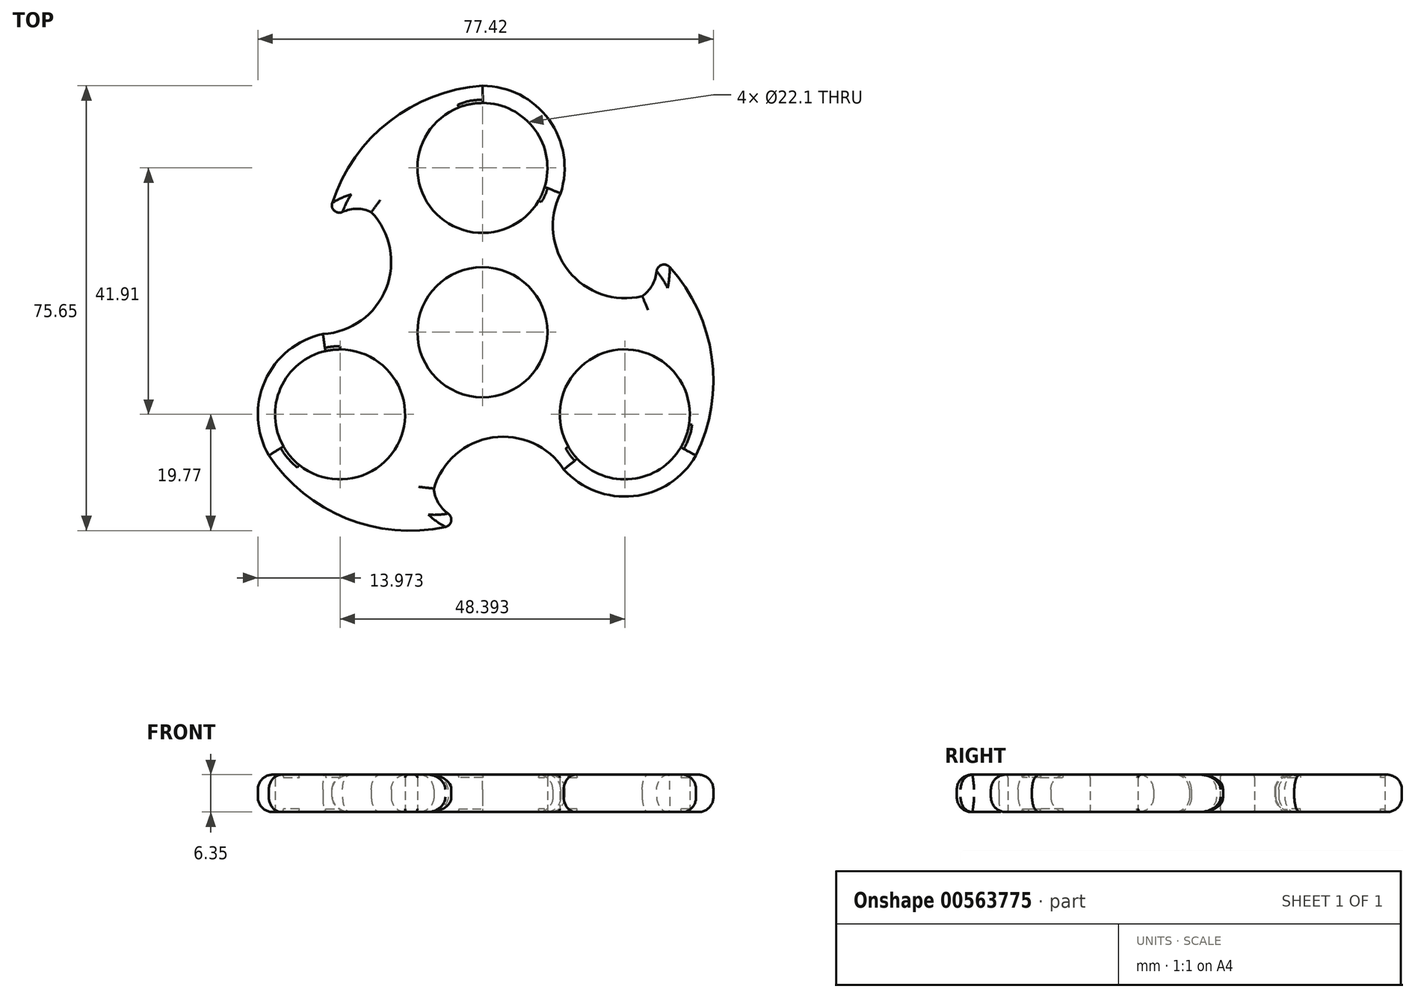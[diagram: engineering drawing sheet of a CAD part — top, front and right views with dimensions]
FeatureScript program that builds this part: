
annotation { "Feature Type Name" : "Feature", "Feature Type Description" : "" }
export const myFeature = defineFeature(function(context is Context, id is Id, definition is map)
    precondition{}
    {
        {
            var Q0;
            Q0=qCreatedBy(makeId("Top.planeOp"),FACE);
            var sketch = newSketch(context, id + "F0", { "sketchPlane" : qUnion([Q0])});
            skCircle(sketch, "E0", {"center": v(0, 0) * mm, "radius": 11.05 * mm});
            skCircle(sketch, "E1", {"center": v(0, 27.94) * mm, "radius": 11.05 * mm});
            skCircle(sketch, "E2.1.0", {"center": v(-24.2, -13.97) * mm, "radius": 11.05 * mm});
            skCircle(sketch, "E2.2.0", {"center": v(24.2, -13.97) * mm, "radius": 11.05 * mm});
            skArc(sketch, "E3", {"start": v(12.54, 21.78) * mm, "mid": v(10.8, 36.8) * mm, "end": v(-3.59, 41.44) * mm});
            skArc(sketch, "E4", {"start": v(-25.13, -0.03) * mm, "mid": v(-37.27, -9.05) * mm, "end": v(-34.1, -23.83) * mm});
            skArc(sketch, "E5", {"start": v(12.6, -21.75) * mm, "mid": v(26.47, -27.75) * mm, "end": v(37.68, -17.61) * mm});
            skPoint(sketch, "E6.start.orphan", {"position": v(0, 41.91) * mm});
            skArc(sketch, "E7", {"start": v(-18.88, 20.44) * mm, "mid": v(-23.33, 20.64) * mm, "end": v(-26.57, 17.6) * mm});
            skPoint(sketch, "E8.startSnap0", {"position": v(-15.2, 14.45) * mm});
            skArc(sketch, "E9", {"start": v(0, 41.91) * mm, "mid": v(-17.55, 34.4) * mm, "end": v(-26.57, 17.6) * mm});
            skArc(sketch, "E10.1.0", {"start": v(-36.3, -20.95) * mm, "mid": v(-21.03, -32.4) * mm, "end": v(-1.95, -31.81) * mm});
            skArc(sketch, "E10.1.1", {"start": v(-8.26, -26.57) * mm, "mid": v(-6.21, -30.52) * mm, "end": v(-1.95, -31.81) * mm});
            skArc(sketch, "E10.2.0", {"start": v(36.3, -20.96) * mm, "mid": v(38.57, -2) * mm, "end": v(28.53, 14.22) * mm});
            skArc(sketch, "E10.2.1", {"start": v(27.14, 6.14) * mm, "mid": v(29.54, 9.88) * mm, "end": v(28.53, 14.22) * mm});
            skArc(sketch, "E11", {"start": v(13.81, -23.32) * mm, "mid": v(1.74, -17.9) * mm, "end": v(-8.26, -26.57) * mm});
            skArc(sketch, "E12.1.0", {"start": v(13.29, 23.62) * mm, "mid": v(14.63, 10.46) * mm, "end": v(27.14, 6.14) * mm});
            skArc(sketch, "E12.2.0", {"start": v(-27.1, -0.3) * mm, "mid": v(-16.37, 7.44) * mm, "end": v(-18.88, 20.44) * mm});
            skPoint(sketch, "E13.end.orphan", {"position": v(-15.2, 4.25) * mm});
            skSolve(sketch);
        }
        {
            var Q0;
            Q0=makeQuery(id+"F0.imprint","IMPRINT",FACE,{"disambiguationData":[TD([[makeQuery(id+"F0.imprint","IMPRINT",EDGE,{"derivedFrom":sQuery(id+"F0.wireOp",EDGE,"E1")}),-1.0]])]});
            var Q1;
            Q1=makeQuery(id+"F0.imprint","IMPRINT",FACE,{"disambiguationData":[TD([[makeQuery(id+"F0.imprint","IMPRINT",EDGE,{"derivedFrom":sQuery(id+"F0.wireOp",EDGE,"E2.2.0")}),-1.0]])]});
            var Q2;
            Q2=makeQuery(id+"F0.imprint","IMPRINT",FACE,{"disambiguationData":[TD([[makeQuery(id+"F0.imprint","IMPRINT",EDGE,{"derivedFrom":sQuery(id+"F0.wireOp",EDGE,"E2.1.0")}),-1.0]])]});
            var Q3;
            Q3=makeQuery(id+"F0.imprint","IMPRINT",FACE,{"disambiguationData":[TD([[makeQuery(id+"F0.imprint","IMPRINT",EDGE,{"derivedFrom":sQuery(id+"F0.wireOp",EDGE,"4O9khdKf-2qk6-6eEU-YUye-EU3OGTiNBHui")}),-1.0]])]});
            var Q4;
            Q4=makeQuery(id+"F0.imprint","IMPRINT",FACE,{"disambiguationData":[TD([[makeQuery(id+"F0.imprint","IMPRINT",EDGE,{"derivedFrom":sQuery(id+"F0.wireOp",EDGE,"E0")}),-1.0]])]});
            extrude(context, id + "F1", {"entities" : qUnion([Q0, Q1, Q2, Q3, Q4]), "depth" : 6.35 * mm});
        }
        {
            var Q0;
            Q0=makeQuery(id+"F1.opExtrude","SWEPT_EDGE",EDGE,{"disambiguationData":[OSD([sQuery(id+"F0.wireOp",EDGE,"E10.1.0"),sQuery(id+"F0.wireOp",EDGE,"E10.1.1")])]});
            var Q1;
            Q1=makeQuery(id+"F1.opExtrude","SWEPT_EDGE",EDGE,{"disambiguationData":[OSD([sQuery(id+"F0.wireOp",EDGE,"E7"),sQuery(id+"F0.wireOp",EDGE,"E9")])]});
            var Q2;
            Q2=makeQuery(id+"F1.opExtrude","SWEPT_EDGE",EDGE,{"disambiguationData":[OSD([sQuery(id+"F0.wireOp",EDGE,"E10.2.0"),sQuery(id+"F0.wireOp",EDGE,"E10.2.1")])]});
            fillet(context, id + "F2", {"entities" : qUnion([Q0, Q1, Q2]), "radius" : 1.27 * mm, "tangentPropagation" : true, "allowEdgeOverflow" : false});
        }
        {
            var Q0;
            Q0=makeQuery(id+"F1.opExtrude","CAP_EDGE",EDGE,{"disambiguationData":[OSD([sQuery(id+"F0.wireOp",EDGE,"E10.1.0")])],"isStart":false});
            var Q1;
            Q1=makeQuery(id+"F1.opExtrude","CAP_EDGE",EDGE,{"disambiguationData":[OSD([sQuery(id+"F0.wireOp",EDGE,"E8")])],"isStart":false});
            var Q2;
            Q2=makeQuery(id+"F1.opExtrude","CAP_EDGE",EDGE,{"disambiguationData":[OSD([sQuery(id+"F0.wireOp",EDGE,"E13")])],"isStart":false});
            var Q3;
            Q3=makeQuery(id+"F1.opExtrude","CAP_EDGE",EDGE,{"disambiguationData":[OSD([sQuery(id+"F0.wireOp",EDGE,"E9")])],"isStart":false});
            var Q4;
            Q4=makeQuery(id+"F1.opExtrude","CAP_EDGE",EDGE,{"disambiguationData":[OSD([sQuery(id+"F0.wireOp",EDGE,"E3")])],"isStart":false});
            var Q5;
            Q5=makeQuery(id+"F1.opExtrude","CAP_EDGE",EDGE,{"disambiguationData":[OSD([sQuery(id+"F0.wireOp",EDGE,"E10.2.3")])],"isStart":false});
            var Q6;
            Q6=makeQuery(id+"F1.opExtrude","CAP_EDGE",EDGE,{"disambiguationData":[OSD([sQuery(id+"F0.wireOp",EDGE,"E10.2.2")])],"isStart":false});
            var Q7;
            Q7=makeQuery(id+"F1.opExtrude","CAP_EDGE",EDGE,{"disambiguationData":[OSD([sQuery(id+"F0.wireOp",EDGE,"E10.2.1")])],"isStart":false});
            var Q8;
            Q8=makeQuery(id+"F1.opExtrude","CAP_EDGE",EDGE,{"disambiguationData":[OSD([sQuery(id+"F0.wireOp",EDGE,"E10.1.2")])],"isStart":false});
            var Q9;
            Q9=makeQuery(id+"F1.opExtrude","CAP_EDGE",EDGE,{"disambiguationData":[OSD([sQuery(id+"F0.wireOp",EDGE,"E10.1.1")])],"isStart":false});
            var Q10;
            Q10=makeQuery(id+"F1.opExtrude","CAP_EDGE",EDGE,{"disambiguationData":[OSD([sQuery(id+"F0.wireOp",EDGE,"E10.2.0")])],"isStart":false});
            var Q11;
            Q11=makeQuery(id+"F1.opExtrude","CAP_EDGE",EDGE,{"disambiguationData":[OSD([sQuery(id+"F0.wireOp",EDGE,"E10.1.3")])],"isStart":false});
            var Q12;
            Q12=makeQuery(id+"F1.opExtrude","CAP_EDGE",EDGE,{"disambiguationData":[OSD([sQuery(id+"F0.wireOp",EDGE,"E7")])],"isStart":false});
            var Q13;
            Q13=makeQuery(id+"F1.opExtrude","CAP_EDGE",EDGE,{"disambiguationData":[OSD([sQuery(id+"F0.wireOp",EDGE,"E10.2.0")])],"isStart":true});
            var Q14;
            Q14=makeQuery(id+"F1.opExtrude","CAP_EDGE",EDGE,{"disambiguationData":[OSD([sQuery(id+"F0.wireOp",EDGE,"E10.2.2")])],"isStart":true});
            var Q15;
            Q15=makeQuery(id+"F1.opExtrude","CAP_EDGE",EDGE,{"disambiguationData":[OSD([sQuery(id+"F0.wireOp",EDGE,"E10.2.3")])],"isStart":true});
            var Q16;
            Q16=makeQuery(id+"F1.opExtrude","CAP_EDGE",EDGE,{"disambiguationData":[OSD([sQuery(id+"F0.wireOp",EDGE,"E9")])],"isStart":true});
            var Q17;
            Q17=makeQuery(id+"F1.opExtrude","CAP_EDGE",EDGE,{"disambiguationData":[OSD([sQuery(id+"F0.wireOp",EDGE,"E8")])],"isStart":true});
            var Q18;
            Q18=makeQuery(id+"F1.opExtrude","CAP_EDGE",EDGE,{"disambiguationData":[OSD([sQuery(id+"F0.wireOp",EDGE,"E13")])],"isStart":true});
            var Q19;
            Q19=makeQuery(id+"F1.opExtrude","CAP_EDGE",EDGE,{"disambiguationData":[OSD([sQuery(id+"F0.wireOp",EDGE,"E10.1.0")])],"isStart":true});
            var Q20;
            Q20=makeQuery(id+"F1.opExtrude","CAP_EDGE",EDGE,{"disambiguationData":[OSD([sQuery(id+"F0.wireOp",EDGE,"E10.1.1")])],"isStart":true});
            var Q21;
            Q21=makeQuery(id+"F1.opExtrude","CAP_EDGE",EDGE,{"disambiguationData":[OSD([sQuery(id+"F0.wireOp",EDGE,"E10.1.2")])],"isStart":true});
            var Q22;
            Q22=makeQuery(id+"F1.opExtrude","CAP_EDGE",EDGE,{"disambiguationData":[OSD([sQuery(id+"F0.wireOp",EDGE,"E10.1.3")])],"isStart":true});
            var Q23;
            Q23=makeQuery(id+"F1.opExtrude","CAP_EDGE",EDGE,{"disambiguationData":[OSD([sQuery(id+"F0.wireOp",EDGE,"E11")])],"isStart":true});
            var Q24;
            Q24=makeQuery(id+"F1.opExtrude","CAP_EDGE",EDGE,{"disambiguationData":[OSD([sQuery(id+"F0.wireOp",EDGE,"E5")])],"isStart":true});
            var Q25;
            Q25=makeQuery(id+"F1.opExtrude","CAP_EDGE",EDGE,{"disambiguationData":[OSD([sQuery(id+"F0.wireOp",EDGE,"E5")])],"isStart":false});
            var Q26;
            Q26=makeQuery(id+"F1.opExtrude","CAP_EDGE",EDGE,{"disambiguationData":[OSD([sQuery(id+"F0.wireOp",EDGE,"E11")])],"isStart":false});
            var Q27;
            Q27=makeQuery(id+"F1.opExtrude","CAP_EDGE",EDGE,{"disambiguationData":[OSD([sQuery(id+"F0.wireOp",EDGE,"E12.2.0")])],"isStart":false});
            var Q28;
            Q28=makeQuery(id+"F1.opExtrude","CAP_EDGE",EDGE,{"disambiguationData":[OSD([sQuery(id+"F0.wireOp",EDGE,"E4")])],"isStart":false});
            var Q29;
            Q29=makeQuery(id+"F1.opExtrude","CAP_EDGE",EDGE,{"disambiguationData":[OSD([sQuery(id+"F0.wireOp",EDGE,"E12.1.0")])],"isStart":false});
            var Q30;
            Q30=makeQuery(id+"F1.opExtrude","CAP_EDGE",EDGE,{"disambiguationData":[OSD([sQuery(id+"F0.wireOp",EDGE,"E12.2.0")])],"isStart":true});
            var Q31;
            Q31=makeQuery(id+"F1.opExtrude","CAP_EDGE",EDGE,{"disambiguationData":[OSD([sQuery(id+"F0.wireOp",EDGE,"E7")])],"isStart":true});
            var Q32;
            Q32=makeQuery(id+"F1.opExtrude","CAP_EDGE",EDGE,{"disambiguationData":[OSD([sQuery(id+"F0.wireOp",EDGE,"E4")])],"isStart":true});
            var Q33;
            Q33=makeQuery(id+"F1.opExtrude","CAP_EDGE",EDGE,{"disambiguationData":[OSD([sQuery(id+"F0.wireOp",EDGE,"E3")])],"isStart":true});
            var Q34;
            Q34=makeQuery(id+"F1.opExtrude","CAP_EDGE",EDGE,{"disambiguationData":[OSD([sQuery(id+"F0.wireOp",EDGE,"E12.1.0")])],"isStart":true});
            var Q35;
            Q35=makeQuery(id+"F1.opExtrude","CAP_EDGE",EDGE,{"disambiguationData":[OSD([sQuery(id+"F0.wireOp",EDGE,"E10.2.1")])],"isStart":true});
            fillet(context, id + "F3", {"entities" : qUnion([Q0, Q1, Q2, Q3, Q4, Q5, Q6, Q7, Q8, Q9, Q10, Q11, Q12, Q13, Q14, Q15, Q16, Q17, Q18, Q19, Q20, Q21, Q22, Q23, Q24, Q25, Q26, Q27, Q28, Q29, Q30, Q31, Q32, Q33, Q34, Q35]), "radius" : 2.54 * mm, "tangentPropagation" : true, "allowEdgeOverflow" : false});
        }
        {
            var Q0;
            Q0=makeQuery(id+"F1.opExtrude","CAP_EDGE",EDGE,{"disambiguationData":[OSD([sQuery(id+"F0.wireOp",EDGE,"E2.1.0")])],"isStart":false});
            var Q1;
            Q1=makeQuery(id+"F1.opExtrude","CAP_EDGE",EDGE,{"disambiguationData":[OSD([sQuery(id+"F0.wireOp",EDGE,"E2.1.0")])],"isStart":true});
            var Q2;
            Q2=makeQuery(id+"F1.opExtrude","CAP_EDGE",EDGE,{"disambiguationData":[OSD([sQuery(id+"F0.wireOp",EDGE,"E0")])],"isStart":true});
            var Q3;
            Q3=makeQuery(id+"F1.opExtrude","CAP_EDGE",EDGE,{"disambiguationData":[OSD([sQuery(id+"F0.wireOp",EDGE,"E0")])],"isStart":false});
            var Q4;
            Q4=makeQuery(id+"F1.opExtrude","CAP_EDGE",EDGE,{"disambiguationData":[OSD([sQuery(id+"F0.wireOp",EDGE,"E1")])],"isStart":true});
            var Q5;
            Q5=makeQuery(id+"F1.opExtrude","CAP_EDGE",EDGE,{"disambiguationData":[OSD([sQuery(id+"F0.wireOp",EDGE,"E1")])],"isStart":false});
            var Q6;
            Q6=makeQuery(id+"F1.opExtrude","CAP_EDGE",EDGE,{"disambiguationData":[OSD([sQuery(id+"F0.wireOp",EDGE,"E2.2.0")])],"isStart":true});
            var Q7;
            Q7=makeQuery(id+"F1.opExtrude","CAP_EDGE",EDGE,{"disambiguationData":[OSD([sQuery(id+"F0.wireOp",EDGE,"E2.2.0")])],"isStart":false});
            fillet(context, id + "F4", {"entities" : qUnion([Q0, Q1, Q2, Q3, Q4, Q5, Q6, Q7]), "radius" : 0.5 * mm, "tangentPropagation" : true, "allowEdgeOverflow" : false});
        }
    });
